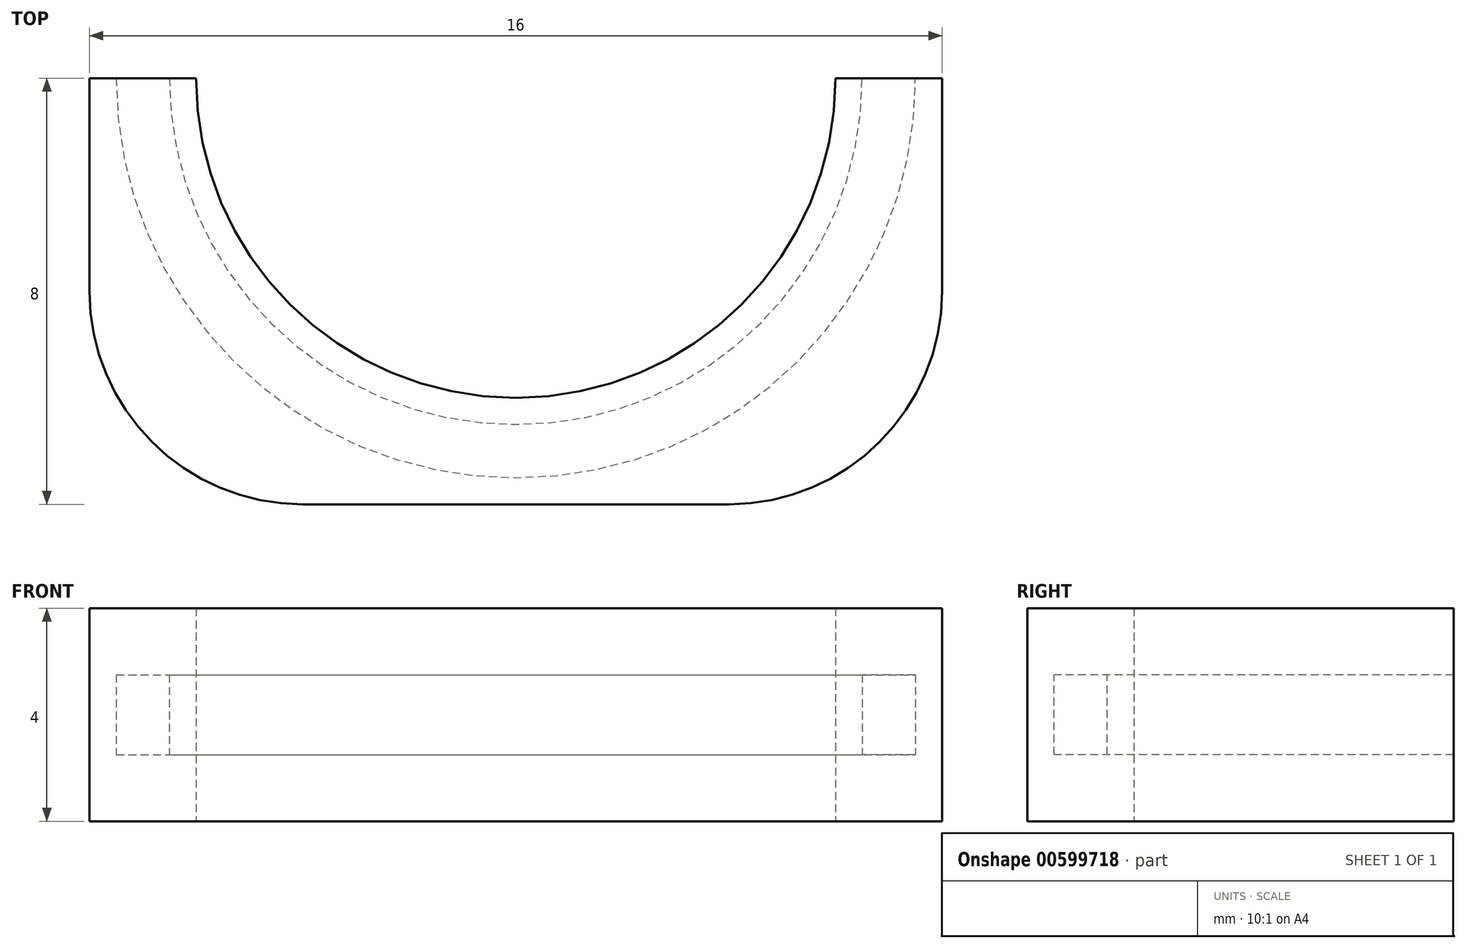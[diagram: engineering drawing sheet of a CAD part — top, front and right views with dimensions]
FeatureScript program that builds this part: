
annotation { "Feature Type Name" : "Feature", "Feature Type Description" : "" }
export const myFeature = defineFeature(function(context is Context, id is Id, definition is map)
    precondition{}
    {
        {
            var Q0;
            Q0=qCreatedBy(makeId("Top.planeOp"),FACE);
            var sketch = newSketch(context, id + "F0", { "sketchPlane" : qUnion([Q0])});
            skLineSegment(sketch, "E0.bottom", {"start": v(0, 0) * mm, "end": v(16, 0) * mm});
            skLineSegment(sketch, "E0.top", {"start": v(0, 8) * mm, "end": v(2, 8) * mm});
            skLineSegment(sketch, "E0.left", {"start": v(0, 0) * mm, "end": v(0, 8) * mm});
            skLineSegment(sketch, "E0.right", {"start": v(16, 0) * mm, "end": v(16, 8) * mm});
            skPoint(sketch, "E1", {"position": v(8, 8) * mm});
            skArc(sketch, "E2", {"start": v(2, 8) * mm, "mid": v(8, 2) * mm, "end": v(14, 8) * mm});
            skLineSegment(sketch, "E3.trimOffspring", {"start": v(14, 8) * mm, "end": v(16, 8) * mm});
            skSolve(sketch);
        }
        {
            var Q0;
            Q0=makeQuery(id+"F0.imprint","IMPRINT",FACE,{"disambiguationData":[TD([[makeQuery(id+"F0.imprint","IMPRINT",EDGE,{"derivedFrom":sQuery(id+"F0.wireOp",EDGE,"E0.bottom")}),1.0]])]});
            extrude(context, id + "F1", {"entities" : qUnion([Q0]), "depth" : 4 * mm, "offsetDistance" : 25 * mm});
        }
        {
            var Q0;
            Q0=makeQuery(id+"F1.opExtrude","SWEPT_EDGE",EDGE,{"disambiguationData":[OSD([sQuery(id+"F0.wireOp",EDGE,"E0.bottom"),sQuery(id+"F0.wireOp",EDGE,"E0.right")])]});
            var Q1;
            Q1=makeQuery(id+"F1.opExtrude","SWEPT_EDGE",EDGE,{"disambiguationData":[OSD([sQuery(id+"F0.wireOp",EDGE,"E0.bottom"),sQuery(id+"F0.wireOp",EDGE,"E0.left")])]});
            fillet(context, id + "F2", {"entities" : qUnion([Q0, Q1]), "radius" : 4 * mm, "tangentPropagation" : true, "allowEdgeOverflow" : false});
        }
        {
            var Q0;
            Q0=makeQuery(id+"F1.opExtrude","CAP_FACE",FACE,{"disambiguationData":[OSD([sQuery(id+"F0.wireOp",EDGE,"E0.bottom"),sQuery(id+"F0.wireOp",EDGE,"E0.top"),sQuery(id+"F0.wireOp",EDGE,"E0.left"),sQuery(id+"F0.wireOp",EDGE,"E0.right"),sQuery(id+"F0.wireOp",EDGE,"E2"),sQuery(id+"F0.wireOp",EDGE,"E3.trimOffspring")])],"isStart":false});
            cPlane(context, id + "F3", {"entities" : qUnion([Q0]), "cplaneType" : CPlaneType.OFFSET, "offset" : 2 * mm, "oppositeDirection" : true, "width" : 150 * mm, "height" : 150 * mm});
        }
        {
            var Q0;
            Q0=qCreatedBy(id+"F3.planeOp",FACE);
            var sketch = newSketch(context, id + "F4", { "sketchPlane" : qUnion([Q0])});
            skLineSegment(sketch, "E4.bottom", {"start": v(0, 0) * mm, "end": v(16, 0) * mm});
            skLineSegment(sketch, "E4.left", {"start": v(0, 0) * mm, "end": v(0, 8) * mm});
            skLineSegment(sketch, "E4.right", {"start": v(16, 0) * mm, "end": v(16, 8) * mm});
            skPoint(sketch, "E5", {"position": v(8, 8) * mm});
            skArc(sketch, "E6", {"start": v(1, 8) * mm, "mid": v(8, 1) * mm, "end": v(15, 8) * mm});
            skSolve(sketch);
        }
        {
            var Q0;
            Q0=makeQuery(id+"F1.opExtrude","SWEPT_FACE",FACE,{"disambiguationData":[OSD([sQuery(id+"F0.wireOp",EDGE,"E0.top")])]});
            var sketch = newSketch(context, id + "F5", { "sketchPlane" : qUnion([Q0])});
            skPoint(sketch, "E7", {"position": v(-1, 2) * mm});
            skPoint(sketch, "E7.positionSnap0", {"position": v(0, 2) * mm});
            skLineSegment(sketch, "E8.bottom", {"start": v(-0.5, 2.75) * mm, "end": v(-1.5, 2.75) * mm});
            skLineSegment(sketch, "E8.top", {"start": v(-0.5, 1.25) * mm, "end": v(-1.5, 1.25) * mm});
            skLineSegment(sketch, "E8.left", {"start": v(-0.5, 2.75) * mm, "end": v(-0.5, 1.25) * mm});
            skLineSegment(sketch, "E8.right", {"start": v(-1.5, 2.75) * mm, "end": v(-1.5, 1.25) * mm});
            skSolve(sketch);
        }
        {
            var Q0;
            Q0=makeQuery(id+"F5.imprint","IMPRINT",FACE,{"disambiguationData":[TD([[makeQuery(id+"F5.imprint","IMPRINT",EDGE,{"derivedFrom":sQuery(id+"F5.wireOp",EDGE,"E8.bottom")}),1.0]])]});
            var Q1;
            Q1=sQuery(id+"F4.wireOp",EDGE,"E6");
            sweep(context, id + "F6", {"operationType" : NewBodyOperationType.REMOVE, "profiles" : qUnion([Q0]), "path" : qUnion([Q1])});
        }
    });
